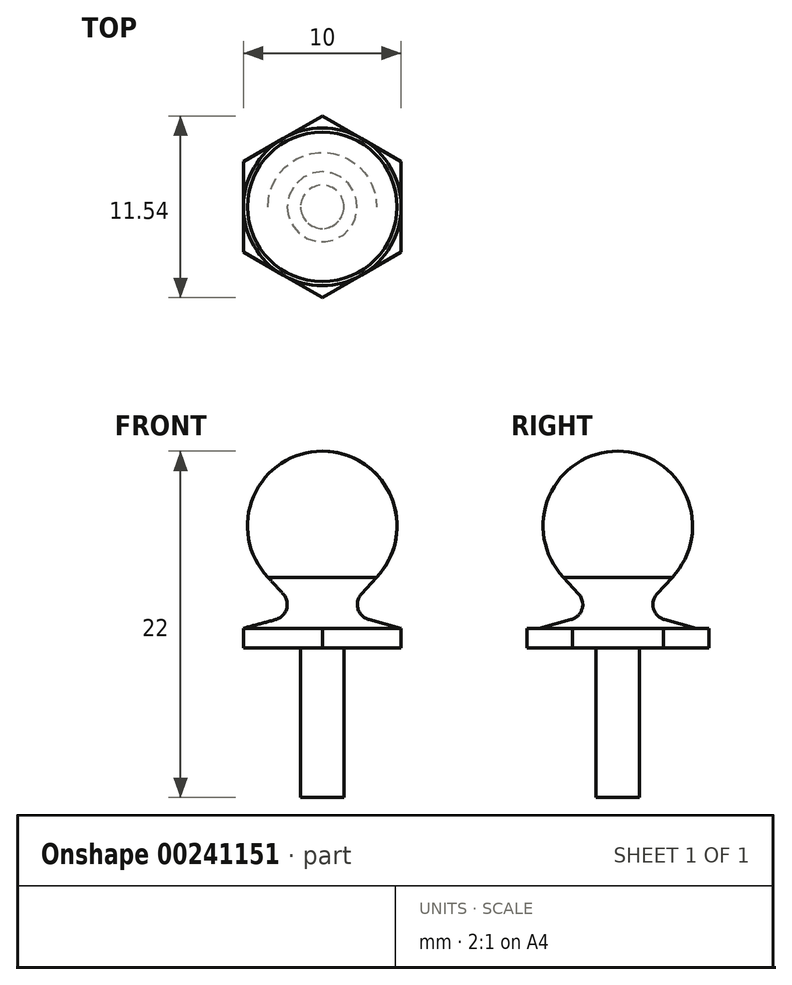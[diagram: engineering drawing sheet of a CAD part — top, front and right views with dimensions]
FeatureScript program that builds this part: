
annotation { "Feature Type Name" : "Feature", "Feature Type Description" : "" }
export const myFeature = defineFeature(function(context is Context, id is Id, definition is map)
    precondition{}
    {
        {
            var Q0;
            Q0=qCreatedBy(makeId("Front.planeOp"),FACE);
            var sketch = newSketch(context, id + "F0", { "sketchPlane" : qUnion([Q0])});
            skArc(sketch, "E0", {"start": v(0, -4.75) * mm, "mid": v(4.75, 0) * mm, "end": v(0, 4.75) * mm});
            skLineSegment(sketch, "E1", {"start": v(0, 4.75) * mm, "end": v(0, -4.75) * mm});
            skSolve(sketch);
        }
        {
            var Q0;
            Q0=makeQuery(id+"F0.imprint","IMPRINT",FACE,{"disambiguationData":[TD([[makeQuery(id+"F0.imprint","IMPRINT",EDGE,{"derivedFrom":sQuery(id+"F0.wireOp",EDGE,"E0")}),1.0]])]});
            var Q1;
            Q1=sQuery(id+"F0.wireOp",EDGE,"E1");
            revolve(context, id + "F1", {"entities" : qUnion([Q0]), "axis" : qUnion([Q1]), "revolveType" : RevolveType.FULL});
        }
        {
            var Q0;
            Q0=qCreatedBy(makeId("Top.planeOp"),FACE);
            var sketch = newSketch(context, id + "F2", { "sketchPlane" : qUnion([Q0])});
            skCircle(sketch, "E2", {"center": v(0, 0) * mm, "radius": 1.38 * mm});
            skSolve(sketch);
        }
        {
            var Q0;
            Q0 = qSketchRegion(id + "F2", true);
            extrude(context, id + "F3", {"entities" : qUnion([Q0]), "operationType" : NewBodyOperationType.ADD, "oppositeDirection" : true, "depth" : (22 - 4.75) * mm});
        }
        {
            var Q0;
            Q0=makeQuery(id+"F3.opExtrude","CAP_FACE",FACE,{"disambiguationData":[OSD([sQuery(id+"F2.wireOp",EDGE,"E2")])],"isStart":false});
            cPlane(context, id + "F4", {"entities" : qUnion([Q0]), "cplaneType" : CPlaneType.OFFSET, "offset" : 9.5 * mm, "oppositeDirection" : true, "width" : 150 * mm, "height" : 150 * mm});
        }
        {
            var Q0;
            Q0=qCreatedBy(id+"F4.planeOp",FACE);
            var sketch = newSketch(context, id + "F5", { "sketchPlane" : qUnion([Q0])});
            skCircle(sketch, "E3.cCircle", {"center": v(0, 0) * mm, "radius": 5 * mm, "construction": true});
            skLineSegment(sketch, "E3.0", {"start": v(5, -2.89) * mm, "end": v(0, -5.77) * mm});
            skLineSegment(sketch, "E3.1", {"start": v(0, -5.77) * mm, "end": v(-5, -2.89) * mm});
            skLineSegment(sketch, "E3.2", {"start": v(-5, -2.89) * mm, "end": v(-5, 2.89) * mm});
            skLineSegment(sketch, "E3.3", {"start": v(-5, 2.89) * mm, "end": v(0, 5.77) * mm});
            skLineSegment(sketch, "E3.4", {"start": v(0, 5.77) * mm, "end": v(5, 2.89) * mm});
            skLineSegment(sketch, "E3.5", {"start": v(5, 2.89) * mm, "end": v(5, -2.89) * mm});
            skPoint(sketch, "E3.0.midPoint", {"position": v(2.5, -4.33) * mm});
            skSolve(sketch);
        }
        {
            var Q0;
            Q0=makeQuery(id+"F5.imprint","IMPRINT",FACE,{"disambiguationData":[TD([[makeQuery(id+"F5.imprint","IMPRINT",EDGE,{"derivedFrom":sQuery(id+"F5.wireOp",EDGE,"E3.0")}),-1.0]])]});
            extrude(context, id + "F6", {"entities" : qUnion([Q0]), "operationType" : NewBodyOperationType.ADD, "oppositeDirection" : true, "depth" : 1.25 * mm});
        }
        {
            var Q0;
            Q0=qCreatedBy(makeId("Front.planeOp"),FACE);
            var sketch = newSketch(context, id + "F7", { "sketchPlane" : qUnion([Q0])});
            skPoint(sketch, "E4.0", {"position": v(5, -6.5) * mm});
            skLineSegment(sketch, "E5", {"start": v(5, -6.5) * mm, "end": v(2.97, -5.95) * mm});
            skLineSegment(sketch, "E6", {"start": v(3.46, -3.26) * mm, "end": v(2.5, -4.3) * mm});
            skArc(sketch, "E7.filletArc", {"start": v(2.5, -4.3) * mm, "mid": v(2.27, -5.27) * mm, "end": v(2.97, -5.95) * mm});
            skLineSegment(sketch, "E8", {"start": v(0, 0) * mm, "end": v(0, 4.75) * mm, "construction": true});
            skLineSegment(sketch, "E9", {"start": v(0, -6.5) * mm, "end": v(0, -4.55) * mm});
            skArc(sketch, "E10", {"start": v(3.46, -3.26) * mm, "mid": v(2.5, -4.04) * mm, "end": v(1.38, -4.55) * mm});
            skLineSegment(sketch, "E11", {"start": v(0, -4.55) * mm, "end": v(1.38, -4.55) * mm});
            skLineSegment(sketch, "E12", {"start": v(2.97, -5.95) * mm, "end": v(1.37, -5.52) * mm, "construction": true});
            skLineSegment(sketch, "E13", {"start": v(1.37, -4.55) * mm, "end": v(1.37, -6.5) * mm, "construction": true});
            skLineSegment(sketch, "E14", {"start": v(5, -6.5) * mm, "end": v(0, -6.5) * mm});
            skArc(sketch, "E15", {"start": v(0, 4.75) * mm, "mid": v(4.7, 0.7) * mm, "end": v(1.37, -4.55) * mm, "construction": true});
            skLineSegment(sketch, "E16", {"start": v(2.5, -4.3) * mm, "end": v(1.37, -5.52) * mm, "construction": true});
            skArc(sketch, "E17", {"start": v(1.37, -4.55) * mm, "mid": v(2.5, -4.04) * mm, "end": v(3.46, -3.26) * mm});
            skSolve(sketch);
        }
        {
            var Q0;
            Q0=makeQuery(id+"F7.imprint","IMPRINT",FACE,{"disambiguationData":[TD([[makeQuery(id+"F7.imprint","IMPRINT",EDGE,{"derivedFrom":sQuery(id+"F7.wireOp",EDGE,"E5")}),1.0]])]});
            var Q1;
            Q1=sQuery(id+"F7.wireOp",EDGE,"E8");
            revolve(context, id + "F8", {"operationType" : NewBodyOperationType.ADD, "entities" : qUnion([Q0]), "axis" : qUnion([Q1]), "revolveType" : RevolveType.FULL});
        }
    });
